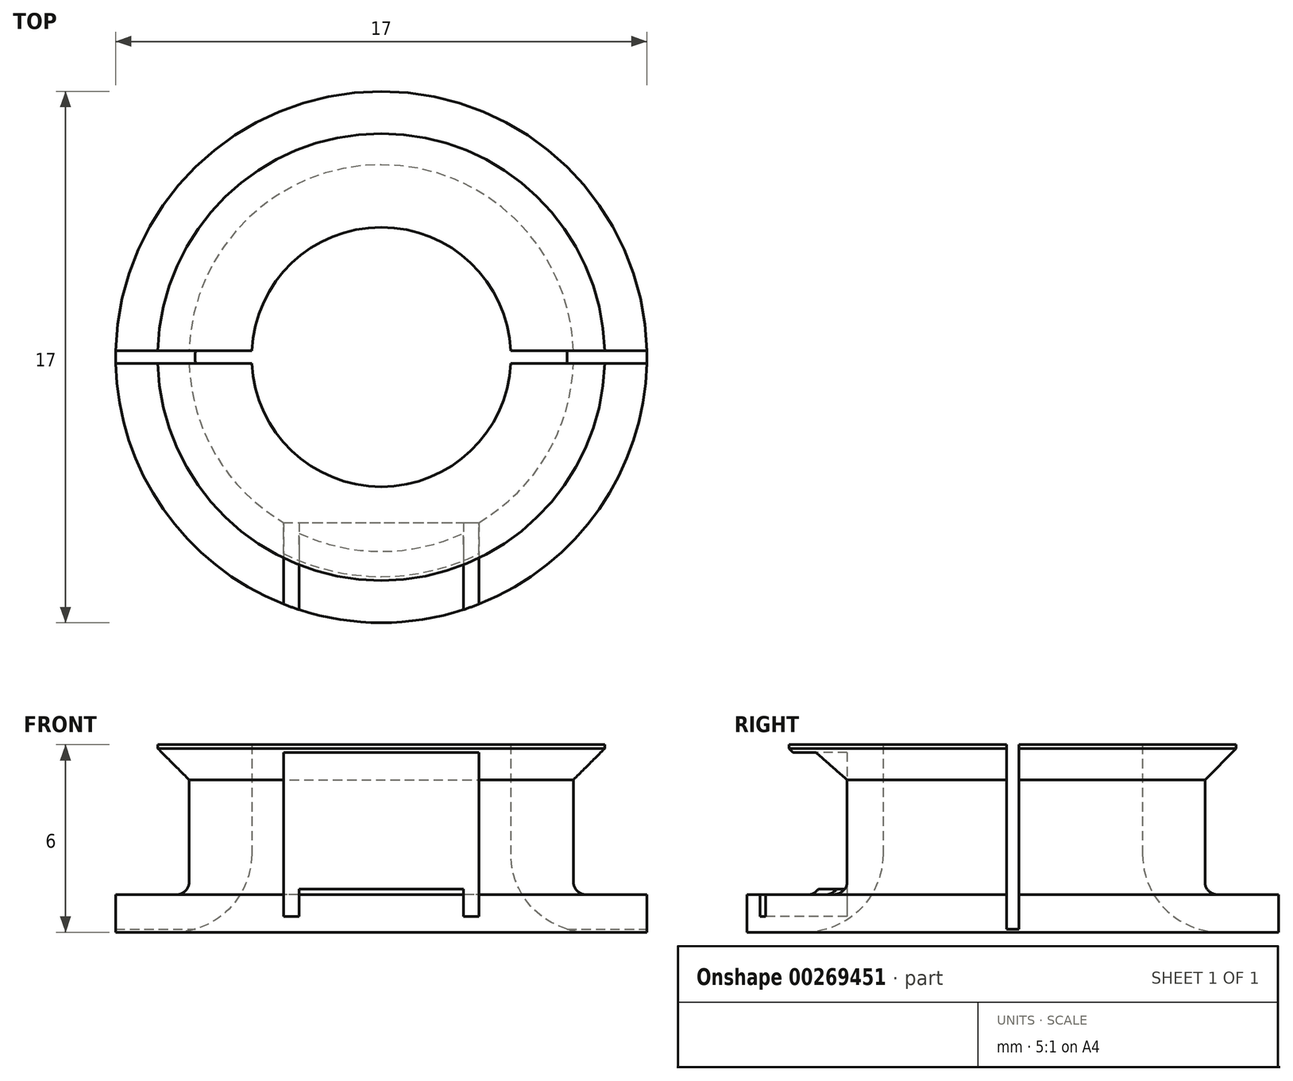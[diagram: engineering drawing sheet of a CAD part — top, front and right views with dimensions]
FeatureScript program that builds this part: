
annotation { "Feature Type Name" : "Feature", "Feature Type Description" : "" }
export const myFeature = defineFeature(function(context is Context, id is Id, definition is map)
    precondition{}
    {
        {
            var Q0;
            Q0=qCreatedBy(makeId("Top.planeOp"),FACE);
            var sketch = newSketch(context, id + "F0", { "sketchPlane" : qUnion([Q0])});
            skCircle(sketch, "E0", {"center": v(0, 0) * mm, "radius": 4.15 * mm});
            skCircle(sketch, "E1", {"center": v(0, 0) * mm, "radius": 6.15 * mm});
            skCircle(sketch, "E2", {"center": v(0, 0) * mm, "radius": 8.5 * mm});
            skSolve(sketch);
        }
        {
            var Q0;
            Q0 = qSketchRegion(id + "F0", true);
            var Q1;
            Q1=makeQuery(id+"F0.imprint","IMPRINT",FACE,{"disambiguationData":[TD([[makeQuery(id+"F0.imprint","IMPRINT",EDGE,{"derivedFrom":sQuery(id+"F0.wireOp",EDGE,"E0")}),-1.0]])]});
            extrude(context, id + "F1", {"entities" : qUnion([Q0, Q1]), "depth" : 1.2 * mm});
        }
        {
            var Q0;
            Q0=makeQuery(id+"F0.imprint","IMPRINT",FACE,{"disambiguationData":[TD([[makeQuery(id+"F0.imprint","IMPRINT",EDGE,{"derivedFrom":sQuery(id+"F0.wireOp",EDGE,"E0")}),-1.0]])]});
            extrude(context, id + "F2", {"entities" : qUnion([Q0]), "operationType" : NewBodyOperationType.ADD, "depth" : 6 * mm});
        }
        {
            var Q0;
            Q0=makeQuery(id+"F1.opExtrude","CAP_EDGE",EDGE,{"disambiguationData":[OSD([sQuery(id+"F0.wireOp",EDGE,"E0")])],"isStart":true});
            fillet(context, id + "F3", {"entities" : qUnion([Q0]), "radius" : 2.5 * mm, "tangentPropagation" : true, "allowEdgeOverflow" : false});
        }
        {
            var Q0;
            Q0=qCreatedBy(makeId("Front.planeOp"),FACE);
            var sketch = newSketch(context, id + "F4", { "sketchPlane" : qUnion([Q0])});
            skLineSegment(sketch, "E3.bottom", {"start": v(-2.63, 5.75) * mm, "end": v(2.63, 5.75) * mm});
            skLineSegment(sketch, "E3.top", {"start": v(-2.63, 0.5) * mm, "end": v(2.63, 0.5) * mm});
            skLineSegment(sketch, "E3.left", {"start": v(-2.62, 5.75) * mm, "end": v(-2.63, 0.5) * mm});
            skLineSegment(sketch, "E3.right", {"start": v(2.63, 5.75) * mm, "end": v(2.62, 0.5) * mm});
            skPoint(sketch, "E4", {"position": v(0, 0.5) * mm});
            skLineSegment(sketch, "E5", {"start": v(0, 0.5) * mm, "end": v(0, 0) * mm, "construction": true});
            skLineSegment(sketch, "E6", {"start": v(-2.63, 3.13) * mm, "end": v(2.62, 3.12) * mm, "construction": true});
            skPoint(sketch, "E7", {"position": v(0, 3.13) * mm});
            skLineSegment(sketch, "E8.bottom", {"start": v(-7, 4.88) * mm, "end": v(7, 4.88) * mm});
            skLineSegment(sketch, "E8.top", {"start": v(-7, 1.38) * mm, "end": v(7, 1.38) * mm});
            skLineSegment(sketch, "E8.left", {"start": v(-7, 4.88) * mm, "end": v(-7, 1.38) * mm});
            skLineSegment(sketch, "E8.right", {"start": v(7, 4.88) * mm, "end": v(7, 1.38) * mm});
            skLineSegment(sketch, "E9.bottom", {"start": v(-3.13, 5.75) * mm, "end": v(3.13, 5.75) * mm});
            skLineSegment(sketch, "E9.top", {"start": v(-3.13, 0.5) * mm, "end": v(3.12, 0.5) * mm});
            skLineSegment(sketch, "E9.left", {"start": v(-3.13, 5.75) * mm, "end": v(-3.13, 0.5) * mm});
            skLineSegment(sketch, "E9.right", {"start": v(3.13, 5.75) * mm, "end": v(3.12, 0.5) * mm});
            skSolve(sketch);
        }
        {
            var Q0;
            Q0=makeQuery(id+"F2.opExtrude","CAP_FACE",FACE,{"disambiguationData":[OSD([sQuery(id+"F0.wireOp",EDGE,"E0"),sQuery(id+"F0.wireOp",EDGE,"E1")])],"isStart":false});
            var sketch = newSketch(context, id + "F5", { "sketchPlane" : qUnion([Q0])});
            skCircle(sketch, "E10", {"center": v(0, 0) * mm, "radius": 7.15 * mm});
            skCircle(sketch, "E11.0", {"center": v(0, 0) * mm, "radius": 6.15 * mm});
            skSolve(sketch);
        }
        {
            var Q0;
            Q0=makeQuery(id+"F5.imprint","IMPRINT",FACE,{"disambiguationData":[TD([[makeQuery(id+"F5.imprint","IMPRINT",EDGE,{"derivedFrom":sQuery(id+"F5.wireOp",EDGE,"E10")}),1.0]])]});
            var Q1;
            Q1=sQuery(id+"F4.wireOp",VERTEX,"E8.bottom.start");
            extrude(context, id + "F6", {"entities" : qUnion([Q0]), "operationType" : NewBodyOperationType.ADD, "endBound" : BoundingType.UP_TO_VERTEX, "oppositeDirection" : true, "endBoundEntityVertex" : qUnion([Q1]), "depth" : 25 * mm});
        }
        {
            var Q0;
            Q0=makeQuery(id+"F6.opExtrude","CAP_EDGE",EDGE,{"disambiguationData":[OSD([sQuery(id+"F5.wireOp",EDGE,"E10")])],"isStart":false});
            chamfer(context, id + "F7", {"entities" : qUnion([Q0]), "width" : 1 * mm, "tangentPropagation" : true});
        }
        {
            var Q0;
            Q0=makeQuery(id+"F2.boolean.opBoolean","INTERSECT",EDGE,{"derivedFrom":[makeQuery(id+"F1.opExtrude","CAP_FACE",FACE,{"disambiguationData":[OSD([sQuery(id+"F0.wireOp",EDGE,"E0"),sQuery(id+"F0.wireOp",EDGE,"E2")])],"isStart":false}),makeQuery(id+"F2.opExtrude","SWEPT_FACE",FACE,{"disambiguationData":[OSD([sQuery(id+"F0.wireOp",EDGE,"E1")])]})]});
            fillet(context, id + "F8", {"entities" : qUnion([Q0]), "radius" : .4 * mm, "tangentPropagation" : true, "allowEdgeOverflow" : false});
        }
        {
            var Q0;
            Q0=qCreatedBy(makeId("Front.planeOp"),FACE);
            cPlane(context, id + "F9", {"entities" : qUnion([Q0]), "cplaneType" : CPlaneType.OFFSET, "offset" : 10 * mm, "width" : 150 * mm, "height" : 150 * mm});
        }
        {
            var Q0;
            Q0=qCreatedBy(id+"F9.planeOp",FACE);
            var sketch = newSketch(context, id + "F10", { "sketchPlane" : qUnion([Q0])});
            skLineSegment(sketch, "E12.0", {"start": v(-2.63, 5.75) * mm, "end": v(2.63, 5.75) * mm});
            skLineSegment(sketch, "E12.1", {"start": v(-2.63, 0.5) * mm, "end": v(2.63, 0.5) * mm});
            skLineSegment(sketch, "E12.2", {"start": v(-2.62, 5.75) * mm, "end": v(-2.63, 0.5) * mm});
            skLineSegment(sketch, "E12.3", {"start": v(2.63, 5.75) * mm, "end": v(2.62, 0.5) * mm});
            skPoint(sketch, "E12.4", {"position": v(0, 0.5) * mm});
            skLineSegment(sketch, "E12.5", {"start": v(0, 0.5) * mm, "end": v(0, 0) * mm});
            skLineSegment(sketch, "E12.6", {"start": v(-2.63, 3.13) * mm, "end": v(2.62, 3.12) * mm});
            skPoint(sketch, "E12.7", {"position": v(0, 3.13) * mm});
            skLineSegment(sketch, "E12.8", {"start": v(-7, 4.88) * mm, "end": v(7, 4.88) * mm});
            skLineSegment(sketch, "E12.9", {"start": v(-7, 1.38) * mm, "end": v(7, 1.38) * mm});
            skLineSegment(sketch, "E12.10", {"start": v(-7, 4.88) * mm, "end": v(-7, 1.38) * mm});
            skLineSegment(sketch, "E12.11", {"start": v(7, 4.88) * mm, "end": v(7, 1.38) * mm});
            skPoint(sketch, "E12.12", {"position": v(0, 3.13) * mm});
            skLineSegment(sketch, "E12.13", {"start": v(-3.13, 5.75) * mm, "end": v(3.13, 5.75) * mm});
            skLineSegment(sketch, "E12.14", {"start": v(-3.13, 0.5) * mm, "end": v(3.12, 0.5) * mm});
            skLineSegment(sketch, "E12.15", {"start": v(-3.13, 5.75) * mm, "end": v(-3.13, 0.5) * mm});
            skLineSegment(sketch, "E12.16", {"start": v(3.13, 5.75) * mm, "end": v(3.12, 0.5) * mm});
            skPoint(sketch, "E12.17", {"position": v(0, 3.13) * mm});
            skSolve(sketch);
        }
        {
            var Q0;
            {var subQ0=sQuery(id+"F10.wireOp",EDGE,"E12.13");var subQ1=sQuery(id+"F10.wireOp",EDGE,"E12.2");var subQ2=makeQuery(id+"F10.imprint","INTERSECT",VERTEX,{"derivedFrom":[subQ1,subQ0]});Q0=makeQuery(id+"F10.imprint","IMPRINT",FACE,{"disambiguationData":[TD([[makeQuery(id+"F10.imprint","IMPRINT",EDGE,{"disambiguationData":[TD([[subQ2,-1.0]])],"derivedFrom":subQ1}),-1.0]])]});}
            var Q1;
            {var subQ3=sQuery(id+"F10.wireOp",EDGE,"E12.2");var subQ8=makeQuery(id+"F10.imprint","INTERSECT",VERTEX,{"derivedFrom":[subQ3,sQuery(id+"F10.wireOp",EDGE,"E12.6")]});Q1=makeQuery(id+"F10.imprint","IMPRINT",FACE,{"disambiguationData":[TD([[makeQuery(id+"F10.imprint","IMPRINT",EDGE,{"disambiguationData":[TD([[subQ8,1.0]])],"derivedFrom":subQ3}),-1.0]])]});}
            var Q2;
            {var subQ0=sQuery(id+"F10.wireOp",EDGE,"E12.6");Q2=makeQuery(id+"F10.imprint","IMPRINT",FACE,{"disambiguationData":[TD([[makeQuery(id+"F10.imprint","IMPRINT",EDGE,{"derivedFrom":subQ0}),1.0]])]});}
            var Q3;
            {var subQ0=sQuery(id+"F10.wireOp",EDGE,"E12.6");Q3=makeQuery(id+"F10.imprint","IMPRINT",FACE,{"disambiguationData":[TD([[makeQuery(id+"F10.imprint","IMPRINT",EDGE,{"derivedFrom":subQ0}),-1.0]])]});}
            var Q4;
            {var subQ0=sQuery(id+"F10.wireOp",EDGE,"E12.13");var subQ1=sQuery(id+"F10.wireOp",EDGE,"E12.2");var subQ2=makeQuery(id+"F10.imprint","INTERSECT",VERTEX,{"derivedFrom":[subQ1,subQ0]});Q4=makeQuery(id+"F10.imprint","IMPRINT",FACE,{"disambiguationData":[TD([[makeQuery(id+"F10.imprint","IMPRINT",EDGE,{"disambiguationData":[TD([[subQ2,-1.0]])],"derivedFrom":subQ1}),1.0]])]});}
            var Q5;
            {var subQ0=sQuery(id+"F10.wireOp",EDGE,"E12.13");var subQ1=sQuery(id+"F10.wireOp",EDGE,"E12.3");var subQ2=makeQuery(id+"F10.imprint","INTERSECT",VERTEX,{"derivedFrom":[subQ1,subQ0]});Q5=makeQuery(id+"F10.imprint","IMPRINT",FACE,{"disambiguationData":[TD([[makeQuery(id+"F10.imprint","IMPRINT",EDGE,{"disambiguationData":[TD([[subQ2,-1.0]])],"derivedFrom":subQ1}),1.0]])]});}
            var Q6;
            {var subQ3=sQuery(id+"F10.wireOp",EDGE,"E12.3");var subQ5=makeQuery(id+"F10.imprint","INTERSECT",VERTEX,{"derivedFrom":[subQ3,sQuery(id+"F10.wireOp",EDGE,"E12.6")]});Q6=makeQuery(id+"F10.imprint","IMPRINT",FACE,{"disambiguationData":[TD([[makeQuery(id+"F10.imprint","IMPRINT",EDGE,{"disambiguationData":[TD([[subQ5,1.0]])],"derivedFrom":subQ3}),1.0]])]});}
            var Q7;
            {var subQ0=sQuery(id+"F10.wireOp",EDGE,"E12.14");var subQ1=sQuery(id+"F10.wireOp",EDGE,"E12.3");var subQ2=makeQuery(id+"F10.imprint","INTERSECT",VERTEX,{"derivedFrom":[subQ1,subQ0]});Q7=makeQuery(id+"F10.imprint","IMPRINT",FACE,{"disambiguationData":[TD([[makeQuery(id+"F10.imprint","IMPRINT",EDGE,{"disambiguationData":[TD([[subQ2,1.0]])],"derivedFrom":subQ1}),1.0]])]});}
            var Q8;
            {var subQ5=sQuery(id+"F10.wireOp",EDGE,"E12.14");var subQ7=makeQuery(id+"F10.imprint","IMPRINT",VERTEX,{"derivedFrom":subQ5});Q8=makeQuery(id+"F10.imprint","IMPRINT",FACE,{"disambiguationData":[TD([[makeQuery(id+"F10.imprint","IMPRINT",EDGE,{"disambiguationData":[TD([[subQ7,1.0]])],"derivedFrom":subQ5}),1.0]])]});}
            var Q9;
            {var subQ0=sQuery(id+"F10.wireOp",EDGE,"E12.14");var subQ1=sQuery(id+"F10.wireOp",EDGE,"E12.2");var subQ2=makeQuery(id+"F10.imprint","INTERSECT",VERTEX,{"derivedFrom":[subQ1,subQ0]});Q9=makeQuery(id+"F10.imprint","IMPRINT",FACE,{"disambiguationData":[TD([[makeQuery(id+"F10.imprint","IMPRINT",EDGE,{"disambiguationData":[TD([[subQ2,1.0]])],"derivedFrom":subQ1}),-1.0]])]});}
            var Q10;
            Q10=makeQuery(id+"F2.opExtrude","SWEPT_FACE",FACE,{"disambiguationData":[OSD([sQuery(id+"F0.wireOp",EDGE,"E1")])]});
            extrude(context, id + "F11", {"entities" : qUnion([Q0, Q1, Q2, Q3, Q4, Q5, Q6, Q7, Q8, Q9]), "operationType" : NewBodyOperationType.REMOVE, "oppositeDirection" : true, "endBoundEntityFace" : qUnion([Q10]), "depth" : (5 - .297) * mm});
        }
        {
            var Q0;
            Q0=makeQuery(id+"F6.boolean.opBoolean","MERGE",FACE,{"derivedFrom":[makeQuery(id+"F2.opExtrude","CAP_FACE",FACE,{"disambiguationData":[OSD([sQuery(id+"F0.wireOp",EDGE,"E0"),sQuery(id+"F0.wireOp",EDGE,"E1")])],"isStart":false}),makeQuery(id+"F6.opExtrude","CAP_FACE",FACE,{"disambiguationData":[OSD([sQuery(id+"F5.wireOp",EDGE,"E10"),sQuery(id+"F5.wireOp",EDGE,"E11.0")])],"isStart":true})]});
            var sketch = newSketch(context, id + "F12", { "sketchPlane" : qUnion([Q0])});
            skLineSegment(sketch, "E13.bottom", {"start": v(-8.5, 0.2) * mm, "end": v(8.5, 0.2) * mm});
            skLineSegment(sketch, "E13.top", {"start": v(-8.5, -0.2) * mm, "end": v(8.5, -0.2) * mm});
            skLineSegment(sketch, "E13.left", {"start": v(-8.5, 0.2) * mm, "end": v(-8.5, -0.2) * mm});
            skLineSegment(sketch, "E13.right", {"start": v(8.5, 0.2) * mm, "end": v(8.5, -0.2) * mm});
            skPoint(sketch, "E13.middle", {"position": v(0, 0) * mm});
            skSolve(sketch);
        }
        {
            var Q0;
            Q0 = qSketchRegion(id + "F12", true);
            extrude(context, id + "F13", {"entities" : qUnion([Q0]), "operationType" : NewBodyOperationType.REMOVE, "oppositeDirection" : true, "depth" : 5.9 * mm});
        }
    });
